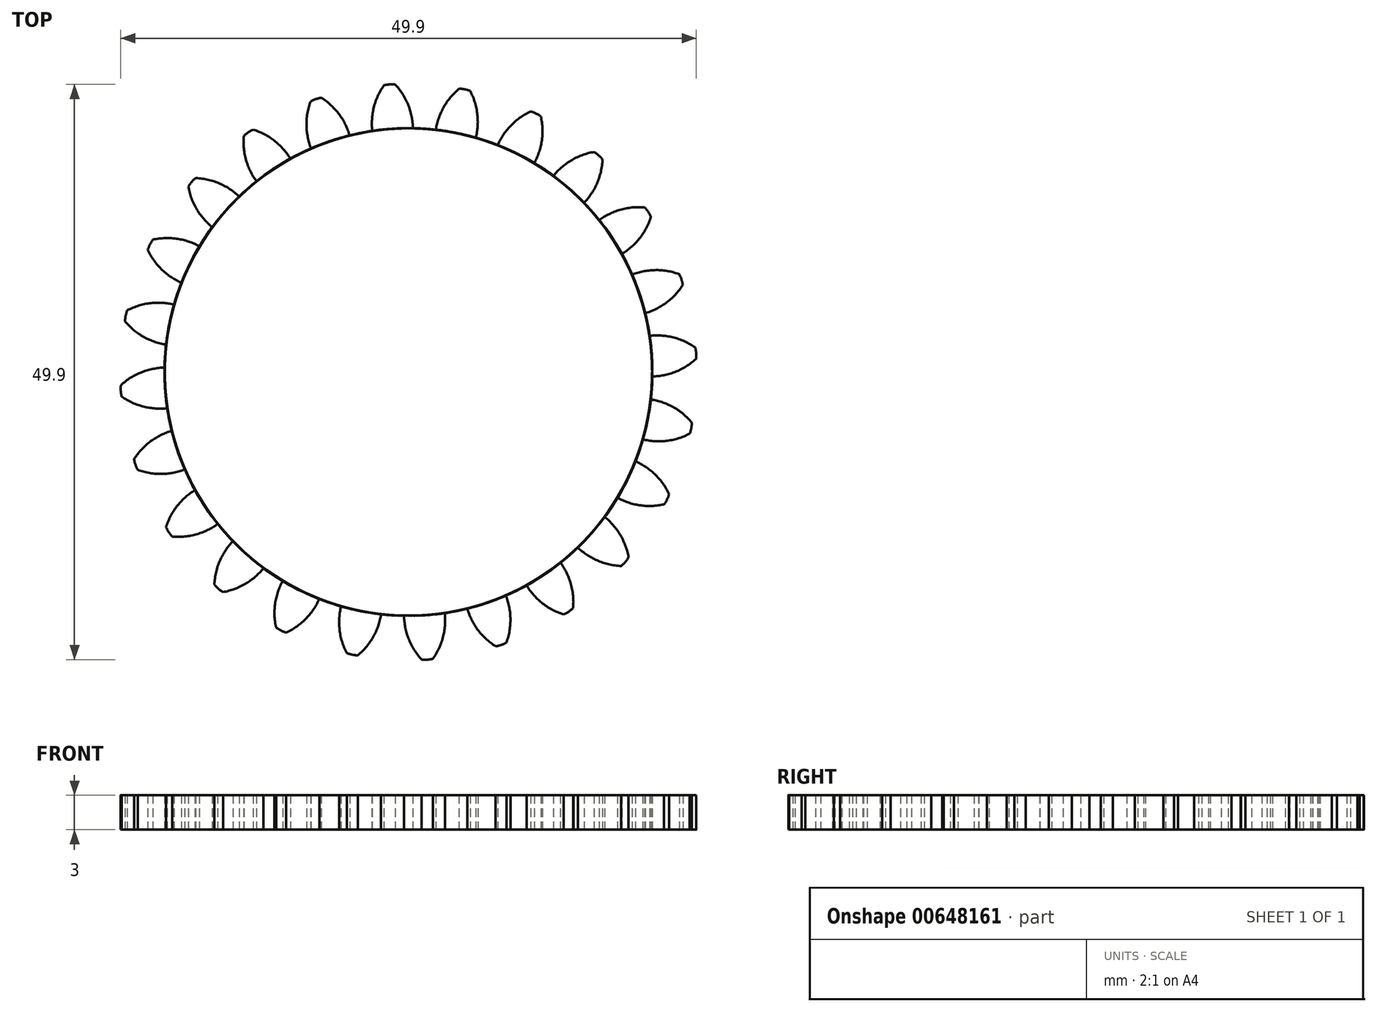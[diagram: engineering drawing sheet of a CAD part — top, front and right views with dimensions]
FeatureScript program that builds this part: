
annotation { "Feature Type Name" : "Feature", "Feature Type Description" : "" }
export const myFeature = defineFeature(function(context is Context, id is Id, definition is map)
    precondition{}
    {
        {
            var Q0;
            Q0=qCreatedBy(makeId("Top.planeOp"),FACE);
            var sketch = newSketch(context, id + "F0", { "sketchPlane" : qUnion([Q0])});
            skCircle(sketch, "E0", {"center": v(0, 0) * mm, "radius": 21.15 * mm});
            skCircle(sketch, "E1", {"center": v(0, 0) * mm, "radius": 23.1 * mm, "construction": true});
            skCircle(sketch, "E2", {"center": v(0, 0) * mm, "radius": 25 * mm, "construction": true});
            skLineSegment(sketch, "E3", {"start": v(0, 0) * mm, "end": v(0, 40.12) * mm, "construction": true});
            skLineSegment(sketch, "E4", {"start": v(0, 0) * mm, "end": v(-2.52, 38.4) * mm, "construction": true});
            skLineSegment(sketch, "E5", {"start": v(0, 23.1) * mm, "end": v(-27.19, 23.1) * mm, "construction": true});
            skLineSegment(sketch, "E6", {"start": v(0, 23.1) * mm, "end": v(-44.25, 7) * mm, "construction": true});
            skCircle(sketch, "E7", {"center": v(0, 0) * mm, "radius": 21.7 * mm, "construction": true});
            skCircle(sketch, "E8", {"center": v(0, 23.1) * mm, "radius": 5.75 * mm, "construction": true});
            skCircle(sketch, "E9", {"center": v(-5.36, 21.03) * mm, "radius": 5.75 * mm, "construction": true});
            skArc(sketch, "E10", {"start": v(0, 23.1) * mm, "mid": v(-0.48, 24.07) * mm, "end": v(-1.14, 24.94) * mm});
            skArc(sketch, "E11", {"start": v(0.38, 21.15) * mm, "mid": v(0.28, 22.14) * mm, "end": v(0, 23.1) * mm});
            skArc(sketch, "E12.MirrorCS", {"start": v(-3.02, 22.9) * mm, "mid": v(-2.66, 23.93) * mm, "end": v(-2.12, 24.87) * mm});
            skArc(sketch, "E13.MirrorCS", {"start": v(-3.14, 20.92) * mm, "mid": v(-3.16, 21.91) * mm, "end": v(-3.02, 22.9) * mm});
            skArc(sketch, "E14", {"start": v(-1.14, 24.94) * mm, "mid": v(-1.64, 24.95) * mm, "end": v(-2.12, 24.87) * mm});
            skSolve(sketch);
        }
        {
            var Q0;
            {var subQ0=sQuery(id+"F0.wireOp",EDGE,"E0");var subQ1=makeQuery(id+"F0.imprint","INTERSECT",VERTEX,{"derivedFrom":[subQ0,sQuery(id+"F0.wireOp",EDGE,"E11")]});Q0=makeQuery(id+"F0.imprint","IMPRINT",FACE,{"disambiguationData":[TD([[makeQuery(id+"F0.imprint","IMPRINT",EDGE,{"disambiguationData":[TD([[subQ1,-1.0]])],"derivedFrom":subQ0}),1.0]])]});}
            var Q1;
            Q1=makeQuery(id+"F0.imprint","IMPRINT",FACE,{"disambiguationData":[TD([[makeQuery(id+"F0.imprint","IMPRINT",EDGE,{"derivedFrom":sQuery(id+"F0.wireOp",EDGE,"E10")}),1.0]])]});
            extrude(context, id + "F1", {"entities" : qUnion([Q0, Q1]), "depth" : 3 * mm, "offsetDistance" : 25 * mm});
        }
        {
            var Q0;
            Q0=makeQuery(id+"F1.opExtrude","SWEPT_BODY",BODY,{"disambiguationData":[OSD([sQuery(id+"F0.wireOp",EDGE,"E0"),sQuery(id+"F0.wireOp",EDGE,"E10"),sQuery(id+"F0.wireOp",EDGE,"E11"),sQuery(id+"F0.wireOp",EDGE,"E12.MirrorCS"),sQuery(id+"F0.wireOp",EDGE,"E13.MirrorCS"),sQuery(id+"F0.wireOp",EDGE,"E14")])]});
            var Q1;
            Q1=makeQuery(id+"F1.opExtrude","SWEPT_FACE",FACE,{"disambiguationData":[OSD([sQuery(id+"F0.wireOp",EDGE,"E0")])]});
            circularPattern(context, id + "F2", {"entities" : qUnion([Q0]), "axis" : qUnion([Q1]), "angle" : 360 * degree, "instanceCount" : 24, "equalSpace" : true});
        }
    });
